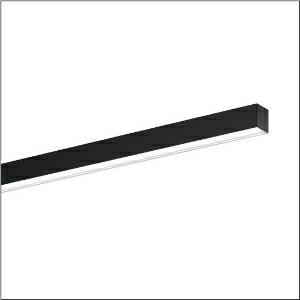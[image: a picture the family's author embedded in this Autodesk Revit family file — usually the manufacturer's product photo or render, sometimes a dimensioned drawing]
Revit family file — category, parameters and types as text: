
# Revit family: silica_r__21_51mx20db42bb_5dab
name_source: partatom
category: Lighting Fixtures
units: mm (PartAtom-declared; Revit-internal decimal feet)

## family parameters
Cut with Voids When Loaded = No
Host = Face
Light Source = No
Part Type = Normal
Room Calculation Point = No
Round Connector Dimension = Use Diameter
Shared = No

## types (1)
- --- (1 x LED, 3000 lm, 19 W, 4000K)
    Apparent Load = 19 VA
    CIE Flux Codes = 48 79 96 100 100
    Color Rendering = 80
    Color Temperature = 4000K
    Default Elevation = 1800 mm
    Description = Silica® 21, office luminaire, primary optical cover: cover, of PMMA, opal, light emission: direct distribution, primary light characteristic: symmetric, installation type: surface-mounted, LED, rated luminous flux: 3.000lm, luminous efficacy: 158lm/W, light colour: 840, colour temperature: 4000K, control gear: DALI 2, with terminal, 3+2-pole, max. 2.5mm², mains connection: 220..240V, AC, 50/60Hz, rated input power: 19W, luminaire housing, of aluminium, matt jet black (RAL 9005), length: 1.504mm, width: 53mm, height: 53mm, protection rating (complete): IP20, insulation class (complete): insulation class I (protective earthing), certification: CE, permissible operating ambient temperature: 0..+35°C, standard: EN 50419, packaging unit: 1 piece
    Height = 53 mm
    Lamp = 1 x LED
    Lamp Light Flux = 3000 lm
    Lamp Power = 19 W
    Lamp count = 1
    Length = 1504 mm
    Luminous efficacy = 158 lm/W
    Manufacturer = Siteco
    ModVariant = No
    Model = 51MX20DB42BB
    Mounting Place = Ceiling
    Mounting Type = Surface mounted
    Number of Poles = 1
    OnlyDefault = Yes
    Power Factor = 1
    Product Name = Silica® 21
    Product group = office luminaire | ceiling mounted
    ProductGroupID = 302
    Protection Class = Protection class I
    Protection Degree = IP 20
    RLX_Detail_Level = 1
    RLX_Emergency_Light_Flux = 0 lm
    RLX_Emergency_Type = 0
    RLX_Emergency_Type_DB = No
    RlxData = <blob elided: 28737 chars, md5=cbc8564a>
    Socket = socket
    Standby Power = 0 W
    System Light Flux = 3000 lm
    System Power = 19 W
    Type Comments = factory setting: luminous flux: 100 % | dim-lin: 254 | 218 mA
    Type Image = l_1335925.jpg
    URL = http://relux.com
    VarID = @adj_118090
    Voltage = 0 V
    Weight = 0.00 kg
    Width = 53 mm

## geometry (parser evidence)
native form markers: Blend x4, Sweep x9
no freeform markers — native parametric forms only
